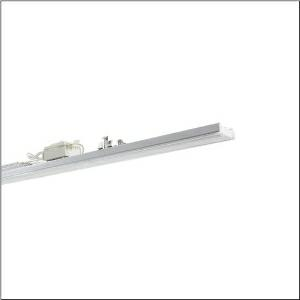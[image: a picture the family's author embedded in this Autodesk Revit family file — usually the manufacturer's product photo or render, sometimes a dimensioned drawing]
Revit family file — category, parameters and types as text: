
# Revit family: licross_r__11_recessed_mo_51te187n485g_a235
name_source: partatom
category: Lighting Fixtures
units: mm (PartAtom-declared; Revit-internal decimal feet)

## family parameters
Cut with Voids When Loaded = No
Host = Face
Light Source = No
Part Type = Normal
Room Calculation Point = No
Round Connector Dimension = Use Diameter
Shared = No

## types (1)
- Licross® 11 Recessed MO (1 x LED, 8700 lm, 48.5 W, 4000K)
    Apparent Load = 49 VA
    CIE Flux Codes = 83 96 99 100 100
    Color Rendering = 80
    Color Temperature = 4000K
    Default Elevation = 1800 mm
    Description = Licross® 11 Recessed MO, luminaire insert, of sheet steel, galvanised, coil coated, white, length: 1.500mm, width: 66mm, height: 67mm, LED rated luminous flux: 8.700lm, light colour: 840, control gear: ON/OFF, with plug, 3-pole, with phase selection, mains connection: 220..240V, AC, 50/60Hz, rated input power: 49W, halogen-free wiring, primary light control with lens, of plastic, primary optical cover: cover, of PMMA, light emission: direct distribution, primary light characteristic: symmetric, protection rating (complete): IP54, insulation class (complete): insulation class I (protective earthing), certification: CE, ENEC, VDE, UKCA, protection symbol: D if used in an environment with non-conductive dust loads with corresponding accessories, impact resistance: IK06, permissible ambient temperature for indoor applications: -35..+35°C, corresponds to IFS (International Featured Standards) requirements for safety and quality in the food industry, reducing of maximum allowable ambient temperature of 5°C with ceiling mounting, packaging unit: 1 piece
    Height = 58 mm
    Lamp = 1 x LED
    Lamp Light Flux = 8700 lm
    Lamp Power = 48.5 W
    Lamp count = 1
    Length = 1500 mm
    Luminous efficacy = 179 lm/W
    Manufacturer = Siteco
    ModVariant = No
    Model = 51TE187N485G
    Mounting Place = Ceiling
    Mounting Type = Pendant
    Number of Poles = 1
    OnlyDefault = Yes
    Power Factor = 1
    Product Name = Licross® 11 Recessed MO
    Product group = luminaire insert
    ProductGroupID = 902
    Protection Class = Protection class I
    Protection Degree = IP 54
    RLX_Detail_Level = 1
    RLX_Emergency_Light_Flux = 0 lm
    RLX_Emergency_Type = 0
    RLX_Emergency_Type_DB = No
    RlxData = <blob elided: 20745 chars, md5=ecf9e6e1>
    Socket = socket
    Standby Power = 0 W
    System Light Flux = 8700 lm
    System Power = 49 W
    Type Comments = Product without accessories
    Type Image = l_1296930.jpg
    URL = http://relux.com
    VarID = ---
    Voltage = 0 V
    Weight = 0.00 kg
    Width = 66 mm

## geometry (parser evidence)
native form markers: Blend x4, Sweep x11
no freeform markers — native parametric forms only
